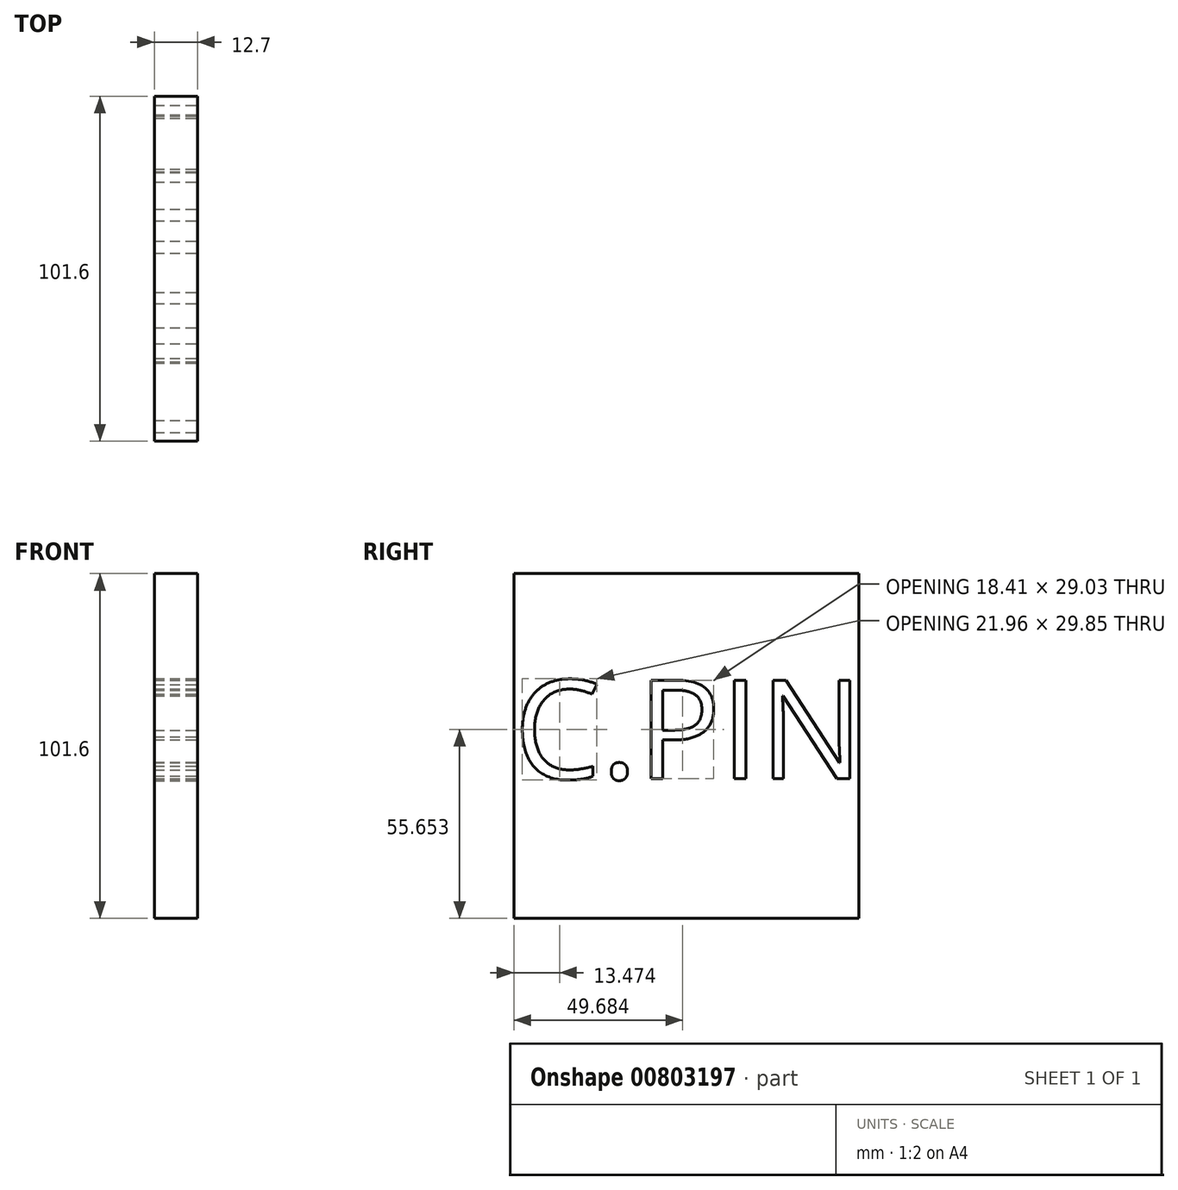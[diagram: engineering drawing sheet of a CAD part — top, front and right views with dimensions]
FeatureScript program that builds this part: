
annotation { "Feature Type Name" : "Feature", "Feature Type Description" : "" }
export const myFeature = defineFeature(function(context is Context, id is Id, definition is map)
    precondition{}
    {
        {
            var Q0;
            Q0=qCreatedBy(makeId("Right.planeOp"),FACE);
            var sketch = newSketch(context, id + "F0", { "sketchPlane" : qUnion([Q0])});
            skLineSegment(sketch, "E0.bottom", {"start": v(-54, 60.07) * mm, "end": v(47.6, 60.07) * mm});
            skLineSegment(sketch, "E0.top", {"start": v(-54, -41.53) * mm, "end": v(47.6, -41.53) * mm});
            skLineSegment(sketch, "E0.left", {"start": v(-54, 60.07) * mm, "end": v(-54, -41.53) * mm});
            skLineSegment(sketch, "E0.right", {"start": v(47.6, 60.07) * mm, "end": v(47.6, -41.53) * mm});
            skSolve(sketch);
        }
        {
            var Q0;
            Q0 = qSketchRegion(id + "F0", true);
            var Q1;
            Q1=makeQuery(id+"F0.imprint","IMPRINT",FACE,{"disambiguationData":[TD([[makeQuery(id+"F0.imprint","IMPRINT",EDGE,{"derivedFrom":sQuery(id+"F0.wireOp",EDGE,"E0.bottom")}),-1.0]])]});
            extrude(context, id + "F1", {"entities" : qUnion([Q0, Q1]), "depth" : 12.7 * mm, "offsetDistance" : 25.4 * mm});
        }
        {
            var Q0;
            Q0=makeQuery(id+"F1.opExtrude","CAP_FACE",FACE,{"disambiguationData":[OSD([sQuery(id+"F0.wireOp",EDGE,"E0.bottom"),sQuery(id+"F0.wireOp",EDGE,"E0.top"),sQuery(id+"F0.wireOp",EDGE,"E0.left"),sQuery(id+"F0.wireOp",EDGE,"E0.right")])],"isStart":false});
            var sketch = newSketch(context, id + "F2", { "sketchPlane" : qUnion([Q0])});
            skText(sketch, "E1", { "text": "C.PIN", "fontName": "OpenSans-Regular.ttf"});
            const initialGuessF2  = {"E1": [-0.054, -0.0004, 1, 0, 0.02928]};
            skSetInitialGuess(sketch, initialGuessF2);
            skSolve(sketch);
        }
        {
            var Q0;
            Q0=makeQuery(id+"F2.imprint","IMPRINT",FACE,{"disambiguationData":[TD([[makeQuery(id+"F2.imprint","IMPRINT",EDGE,{"derivedFrom":sQuery(id+"F2.wireOp",EDGE,"E1.sketch_text.stroke-0")}),-1.0]])]});
            var Q1;
            Q1=makeQuery(id+"F2.imprint","IMPRINT",FACE,{"disambiguationData":[TD([[makeQuery(id+"F2.imprint","IMPRINT",EDGE,{"derivedFrom":sQuery(id+"F2.wireOp",EDGE,"E1.sketch_text.stroke-15")}),-1.0]])]});
            var Q2;
            Q2=makeQuery(id+"F2.imprint","IMPRINT",FACE,{"disambiguationData":[TD([[makeQuery(id+"F2.imprint","IMPRINT",EDGE,{"derivedFrom":sQuery(id+"F2.wireOp",EDGE,"E1.sketch_text.stroke-23")}),-1.0]])]});
            var Q3;
            Q3=makeQuery(id+"F2.imprint","IMPRINT",FACE,{"disambiguationData":[TD([[makeQuery(id+"F2.imprint","IMPRINT",EDGE,{"derivedFrom":sQuery(id+"F2.wireOp",EDGE,"E1.sketch_text.stroke-38")}),-1.0]])]});
            var Q4;
            Q4=makeQuery(id+"F2.imprint","IMPRINT",FACE,{"disambiguationData":[TD([[makeQuery(id+"F2.imprint","IMPRINT",EDGE,{"derivedFrom":sQuery(id+"F2.wireOp",EDGE,"E1.sketch_text.stroke-42")}),-1.0]])]});
            extrude(context, id + "F3", {"entities" : qUnion([Q0, Q1, Q2, Q3, Q4]), "operationType" : NewBodyOperationType.REMOVE, "oppositeDirection" : true, "depth" : 25 * mm, "offsetDistance" : 25 * mm});
        }
    });
